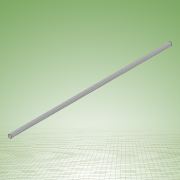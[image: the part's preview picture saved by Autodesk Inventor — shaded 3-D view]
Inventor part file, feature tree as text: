
AUTODESK INVENTOR PART (.ipt)
format: ipt  version: 2022 (Build 260153000, 153)  size: 112,640 bytes
history: native  units: mm
features: other x1, extrude x1, thread x1, sketch x1
ambient origin geometry x8: Origin, YZ Plane, XZ Plane, XY Plane, X Axis, Y Axis, Z Axis, Center Point
bodies: Body1 (feature_tree)
feature tree (4):
  other  "Sólido1"
  extrude  "Extrusión1"  Depth=280.0mm TaperAngle=0.0deg
  thread  "Rosca1"  [1 undecoded]
  sketch  "Boceto1"  dims[d0=6.35mm d1=280.0mm d2=0.0mm d3=200.0mm d4=0.0mm d5=0.5mm d6=0.872665mm d7=0.5mm d8=0.872665mm]
note: 1 required parameter value undecoded (feature->parameter linkage not recoverable at this tier; creation-order binding heuristic only, values carry confidence <= 0.55)
